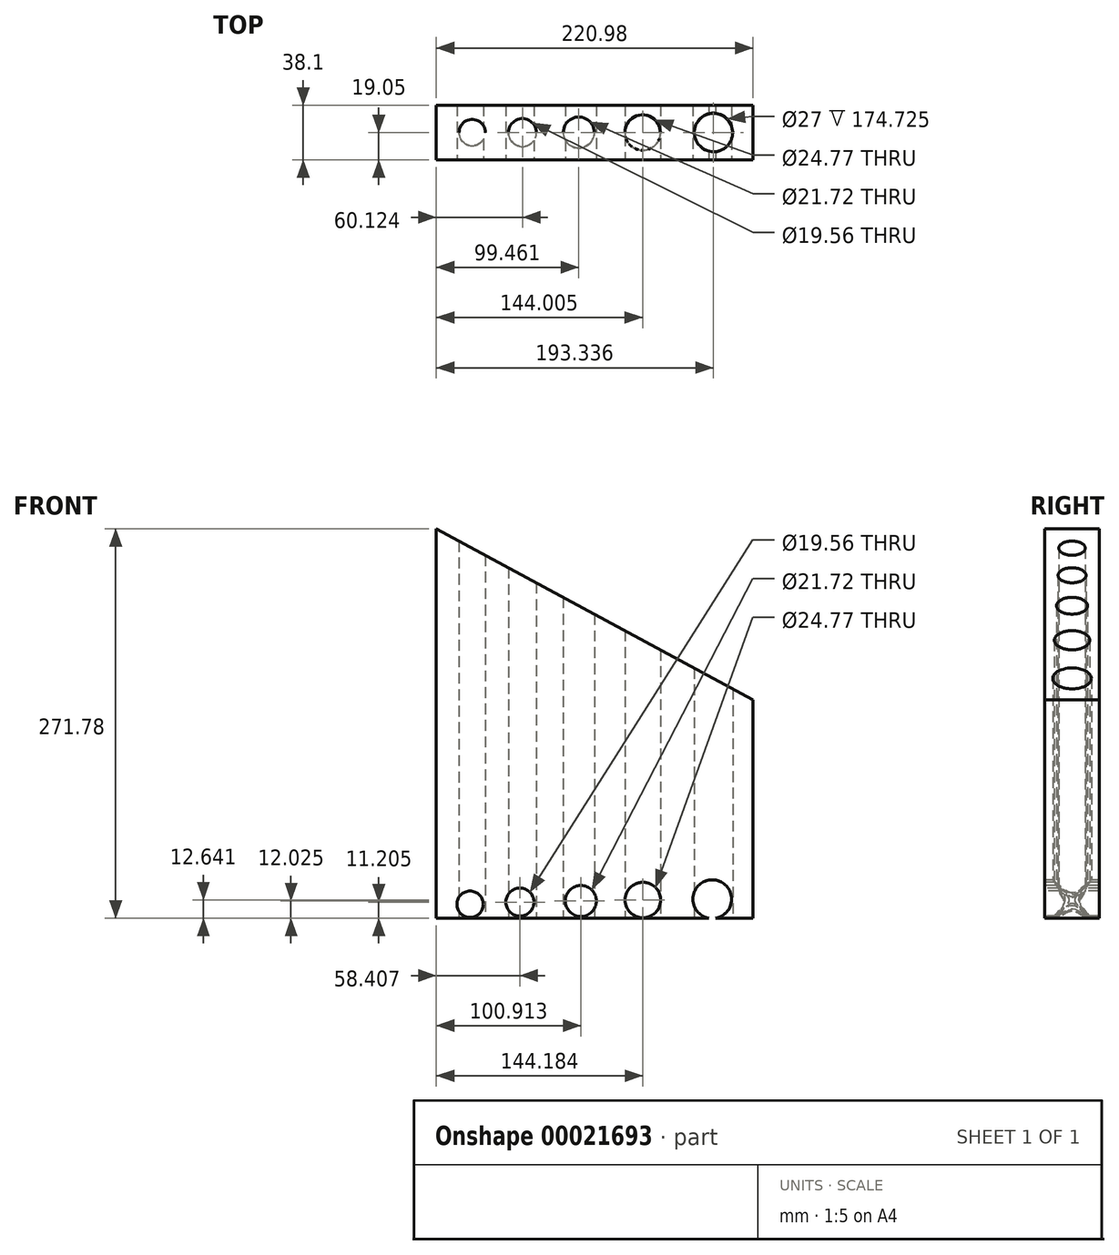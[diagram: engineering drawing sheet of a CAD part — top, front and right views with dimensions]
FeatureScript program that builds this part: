
annotation { "Feature Type Name" : "Feature", "Feature Type Description" : "" }
export const myFeature = defineFeature(function(context is Context, id is Id, definition is map)
    precondition{}
    {
        {
            var Q0;
            Q0=qCreatedBy(makeId("Front.planeOp"),FACE);
            var sketch = newSketch(context, id + "F0", { "sketchPlane" : qUnion([Q0])});
            skLineSegment(sketch, "E0.bottom", {"start": v(-75.01, 96.53) * mm, "end": v(145.97, 96.53) * mm});
            skLineSegment(sketch, "E0.top", {"start": v(-75.01, -55.87) * mm, "end": v(145.97, -55.87) * mm});
            skLineSegment(sketch, "E0.left", {"start": v(-75.01, 96.53) * mm, "end": v(-75.01, -55.87) * mm});
            skLineSegment(sketch, "E0.right", {"start": v(145.97, 96.53) * mm, "end": v(145.97, -55.87) * mm});
            skLineSegment(sketch, "E1", {"start": v(-75.01, 96.53) * mm, "end": v(-75.01, 215.9) * mm});
            skLineSegment(sketch, "E2", {"start": v(-75.01, 215.9) * mm, "end": v(145.97, 96.53) * mm});
            skSolve(sketch);
        }
        {
            var Q0;
            Q0 = qSketchRegion(id + "F0", true);
            extrude(context, id + "F1", {"entities" : qUnion([Q0]), "depth" : 38.1 * mm});
        }
        {
            var Q0;
            Q0=makeQuery(id+"F1.opExtrude","SWEPT_FACE",FACE,{"disambiguationData":[OSD([sQuery(id+"F0.wireOp",EDGE,"E0.top")])]});
            var sketch = newSketch(context, id + "F2", { "sketchPlane" : qUnion([Q0])});
            skLineSegment(sketch, "E3", {"start": v(-75.01, 19.05) * mm, "end": v(145.97, 19.05) * mm});
            skCircle(sketch, "E4", {"center": v(-49.95, 19.05) * mm, "radius": 9.2 * mm});
            skCircle(sketch, "E5", {"center": v(-14.89, 19.05) * mm, "radius": 9.78 * mm});
            skCircle(sketch, "E6", {"center": v(24.45, 19.05) * mm, "radius": 10.86 * mm});
            skCircle(sketch, "E7", {"center": v(118.33, 19.05) * mm, "radius": 14.58 * mm});
            skCircle(sketch, "E8", {"center": v(69, 19.05) * mm, "radius": 12.38 * mm});
            skSolve(sketch);
        }
        {
            var Q0;
            Q0=sQuery(id+"F2.wireOp",VERTEX,"E4.center");
            var Q1;
            Q1=makeQuery(id+"F1.opExtrude","SWEPT_BODY",BODY,{"disambiguationData":[OSD([sQuery(id+"F0.wireOp",EDGE,"E0.top"),sQuery(id+"F0.wireOp",EDGE,"E0.left"),sQuery(id+"F0.wireOp",EDGE,"E0.right"),sQuery(id+"F0.wireOp",EDGE,"E1"),sQuery(id+"F0.wireOp",EDGE,"E2")])]});
            hole(context, id + "F3", {"style" : HoleStyle.SIMPLE, "holeDiameter" : 18.41 * mm, "endStyle" : HoleEndStyle.THROUGH, "locations" : qUnion([Q0]), "scope" : qUnion([Q1])});
        }
        {
            var Q0;
            Q0=sQuery(id+"F2.wireOp",VERTEX,"E5.center");
            var Q1;
            Q1=makeQuery(id+"F1.opExtrude","SWEPT_BODY",BODY,{"disambiguationData":[OSD([sQuery(id+"F0.wireOp",EDGE,"E0.top"),sQuery(id+"F0.wireOp",EDGE,"E0.left"),sQuery(id+"F0.wireOp",EDGE,"E0.right"),sQuery(id+"F0.wireOp",EDGE,"E1"),sQuery(id+"F0.wireOp",EDGE,"E2")])]});
            hole(context, id + "F4", {"style" : HoleStyle.SIMPLE, "holeDiameter" : 19.56 * mm, "endStyle" : HoleEndStyle.THROUGH, "locations" : qUnion([Q0]), "scope" : qUnion([Q1])});
        }
        {
            var Q0;
            Q0=sQuery(id+"F2.wireOp",VERTEX,"E6.center");
            var Q1;
            Q1=makeQuery(id+"F1.opExtrude","SWEPT_BODY",BODY,{"disambiguationData":[OSD([sQuery(id+"F0.wireOp",EDGE,"E0.top"),sQuery(id+"F0.wireOp",EDGE,"E0.left"),sQuery(id+"F0.wireOp",EDGE,"E0.right"),sQuery(id+"F0.wireOp",EDGE,"E1"),sQuery(id+"F0.wireOp",EDGE,"E2")])]});
            hole(context, id + "F5", {"style" : HoleStyle.SIMPLE, "holeDiameter" : 21.72 * mm, "endStyle" : HoleEndStyle.THROUGH, "locations" : qUnion([Q0]), "scope" : qUnion([Q1])});
        }
        {
            var Q0;
            Q0=sQuery(id+"F2.wireOp",VERTEX,"E8.center");
            var Q1;
            Q1=makeQuery(id+"F1.opExtrude","SWEPT_BODY",BODY,{"disambiguationData":[OSD([sQuery(id+"F0.wireOp",EDGE,"E0.top"),sQuery(id+"F0.wireOp",EDGE,"E0.left"),sQuery(id+"F0.wireOp",EDGE,"E0.right"),sQuery(id+"F0.wireOp",EDGE,"E1"),sQuery(id+"F0.wireOp",EDGE,"E2")])]});
            hole(context, id + "F6", {"style" : HoleStyle.SIMPLE, "holeDiameter" : 24.76 * mm, "endStyle" : HoleEndStyle.THROUGH, "locations" : qUnion([Q0]), "scope" : qUnion([Q1])});
        }
        {
            var Q0;
            Q0=makeQuery(id+"F1.opExtrude","CAP_FACE",FACE,{"disambiguationData":[OSD([sQuery(id+"F0.wireOp",EDGE,"E0.top"),sQuery(id+"F0.wireOp",EDGE,"E0.left"),sQuery(id+"F0.wireOp",EDGE,"E0.right"),sQuery(id+"F0.wireOp",EDGE,"E1"),sQuery(id+"F0.wireOp",EDGE,"E2")])],"isStart":false});
            var sketch = newSketch(context, id + "F7", { "sketchPlane" : qUnion([Q0])});
            skCircle(sketch, "E9.cCircle", {"center": v(-51.4, -46.13) * mm, "radius": 9.2 * mm, "construction": true});
            skLineSegment(sketch, "E9.0", {"start": v(-60.6, -55.34) * mm, "end": v(-60.6, -36.93) * mm});
            skLineSegment(sketch, "E9.1", {"start": v(-60.6, -36.93) * mm, "end": v(-42.2, -36.93) * mm});
            skLineSegment(sketch, "E9.2", {"start": v(-42.2, -36.93) * mm, "end": v(-42.2, -55.34) * mm});
            skLineSegment(sketch, "E9.3", {"start": v(-42.2, -55.34) * mm, "end": v(-60.6, -55.34) * mm});
            skPoint(sketch, "E9.0.midPoint", {"position": v(-60.6, -46.13) * mm});
            skLineSegment(sketch, "E10.1", {"start": v(-26.37, -35.69) * mm, "end": v(-6.81, -35.69) * mm});
            skLineSegment(sketch, "E10.2", {"start": v(-6.81, -35.69) * mm, "end": v(-6.81, -55.25) * mm});
            skLineSegment(sketch, "E10.3", {"start": v(-6.81, -55.25) * mm, "end": v(-26.37, -55.25) * mm});
            skLineSegment(sketch, "E10.0", {"start": v(-26.37, -55.25) * mm, "end": v(-26.37, -35.69) * mm});
            skLineSegment(sketch, "E11.1", {"start": v(19.17, 93.32) * mm, "end": v(20.43, 93.32) * mm});
            skLineSegment(sketch, "E12.1", {"start": v(56.78, -30.08) * mm, "end": v(81.55, -30.08) * mm});
            skLineSegment(sketch, "E12.2", {"start": v(81.55, -30.08) * mm, "end": v(81.55, -54.84) * mm});
            skLineSegment(sketch, "E12.3", {"start": v(81.55, -54.84) * mm, "end": v(56.78, -54.84) * mm});
            skLineSegment(sketch, "E12.0", {"start": v(56.78, -54.84) * mm, "end": v(56.78, -30.08) * mm});
            skLineSegment(sketch, "E13.1", {"start": v(14.32, -32.98) * mm, "end": v(36.04, -32.98) * mm});
            skLineSegment(sketch, "E13.2", {"start": v(36.04, -32.98) * mm, "end": v(36.04, -54.7) * mm});
            skLineSegment(sketch, "E13.3", {"start": v(36.04, -54.7) * mm, "end": v(14.32, -54.7) * mm});
            skLineSegment(sketch, "E13.0", {"start": v(14.32, -54.7) * mm, "end": v(14.32, -32.98) * mm});
            skLineSegment(sketch, "E14.bottom", {"start": v(104.2, -28.87) * mm, "end": v(131.2, -28.87) * mm});
            skLineSegment(sketch, "E14.top", {"start": v(104.2, -55.87) * mm, "end": v(131.2, -55.87) * mm});
            skLineSegment(sketch, "E14.left", {"start": v(104.2, -28.87) * mm, "end": v(104.2, -55.87) * mm});
            skLineSegment(sketch, "E14.right", {"start": v(131.2, -28.87) * mm, "end": v(131.2, -55.87) * mm});
            skSolve(sketch);
        }
        {
            var Q0;
            Q0=sQuery(id+"F2.wireOp",VERTEX,"E7.center");
            var Q1;
            Q1=makeQuery(id+"F1.opExtrude","SWEPT_BODY",BODY,{"disambiguationData":[OSD([sQuery(id+"F0.wireOp",EDGE,"E0.top"),sQuery(id+"F0.wireOp",EDGE,"E0.left"),sQuery(id+"F0.wireOp",EDGE,"E0.right"),sQuery(id+"F0.wireOp",EDGE,"E1"),sQuery(id+"F0.wireOp",EDGE,"E2")])]});
            hole(context, id + "F8", {"style" : HoleStyle.SIMPLE, "holeDiameter" : 27 * mm, "endStyle" : HoleEndStyle.THROUGH, "locations" : qUnion([Q0]), "scope" : qUnion([Q1])});
        }
        {
            var Q0;
            Q0=sQuery(id+"F7.wireOp",VERTEX,"E9.cCircle.center");
            var Q1;
            Q1=makeQuery(id+"F1.opExtrude","SWEPT_BODY",BODY,{"disambiguationData":[OSD([sQuery(id+"F0.wireOp",EDGE,"E0.top"),sQuery(id+"F0.wireOp",EDGE,"E0.left"),sQuery(id+"F0.wireOp",EDGE,"E0.right"),sQuery(id+"F0.wireOp",EDGE,"E1"),sQuery(id+"F0.wireOp",EDGE,"E2")])]});
            hole(context, id + "F9", {"style" : HoleStyle.SIMPLE, "holeDiameter" : 18.41 * mm, "endStyle" : HoleEndStyle.THROUGH, "locations" : qUnion([Q0]), "scope" : qUnion([Q1])});
        }
        {
            var Q0;
            Q0=makeQuery(id+"F7.imprint","IMPRINT",FACE,{"disambiguationData":[TD([[makeQuery(id+"F7.imprint","IMPRINT",EDGE,{"derivedFrom":sQuery(id+"F7.wireOp",EDGE,"E9.0")}),1.0]])]});
            var sketch = newSketch(context, id + "F10", { "sketchPlane" : qUnion([Q0])});
            skLineSegment(sketch, "E15", {"start": v(-7.55, -35.94) * mm, "end": v(-25.65, -53.4) * mm});
            skLineSegment(sketch, "E16", {"start": v(-7.55, -54.04) * mm, "end": v(-25.65, -37.23) * mm});
            skPoint(sketch, "E17", {"position": v(-16.6, -44.67) * mm});
            skLineSegment(sketch, "E18", {"start": v(14.42, -55.33) * mm, "end": v(36.4, -33.35) * mm});
            skLineSegment(sketch, "E19", {"start": v(37.04, -55.33) * mm, "end": v(16.36, -34) * mm});
            skLineSegment(sketch, "E20", {"start": v(56.43, -55.98) * mm, "end": v(80.99, -31.42) * mm});
            skLineSegment(sketch, "E21", {"start": v(56.43, -29.48) * mm, "end": v(80.99, -55.98) * mm});
            skLineSegment(sketch, "E22", {"start": v(104.25, -57.27) * mm, "end": v(128.81, -30.12) * mm});
            skLineSegment(sketch, "E23", {"start": v(102.32, -28.83) * mm, "end": v(134.49, -57.94) * mm});
            skPoint(sketch, "E24", {"position": v(25.9, -43.84) * mm});
            skPoint(sketch, "E25", {"position": v(69.17, -43.23) * mm});
            skPoint(sketch, "E26", {"position": v(117.53, -42.6) * mm});
            skSolve(sketch);
        }
        {
            var Q0;
            Q0=sQuery(id+"F10.wireOp",VERTEX,"E17");
            var Q1;
            Q1=makeQuery(id+"F1.opExtrude","SWEPT_BODY",BODY,{"disambiguationData":[OSD([sQuery(id+"F0.wireOp",EDGE,"E0.top"),sQuery(id+"F0.wireOp",EDGE,"E0.left"),sQuery(id+"F0.wireOp",EDGE,"E0.right"),sQuery(id+"F0.wireOp",EDGE,"E1"),sQuery(id+"F0.wireOp",EDGE,"E2")])]});
            hole(context, id + "F11", {"style" : HoleStyle.SIMPLE, "holeDiameter" : 19.56 * mm, "endStyle" : HoleEndStyle.THROUGH, "locations" : qUnion([Q0]), "scope" : qUnion([Q1])});
        }
        {
            var Q0;
            Q0=sQuery(id+"F10.wireOp",VERTEX,"E24");
            var Q1;
            Q1=makeQuery(id+"F1.opExtrude","SWEPT_BODY",BODY,{"disambiguationData":[OSD([sQuery(id+"F0.wireOp",EDGE,"E0.top"),sQuery(id+"F0.wireOp",EDGE,"E0.left"),sQuery(id+"F0.wireOp",EDGE,"E0.right"),sQuery(id+"F0.wireOp",EDGE,"E1"),sQuery(id+"F0.wireOp",EDGE,"E2")])]});
            hole(context, id + "F12", {"style" : HoleStyle.SIMPLE, "holeDiameter" : 21.72 * mm, "endStyle" : HoleEndStyle.THROUGH, "locations" : qUnion([Q0]), "scope" : qUnion([Q1])});
        }
        {
            var Q0;
            Q0=sQuery(id+"F10.wireOp",VERTEX,"E25");
            var Q1;
            Q1=makeQuery(id+"F1.opExtrude","SWEPT_BODY",BODY,{"disambiguationData":[OSD([sQuery(id+"F0.wireOp",EDGE,"E0.top"),sQuery(id+"F0.wireOp",EDGE,"E0.left"),sQuery(id+"F0.wireOp",EDGE,"E0.right"),sQuery(id+"F0.wireOp",EDGE,"E1"),sQuery(id+"F0.wireOp",EDGE,"E2")])]});
            hole(context, id + "F13", {"style" : HoleStyle.SIMPLE, "holeDiameter" : 24.76 * mm, "endStyle" : HoleEndStyle.THROUGH, "locations" : qUnion([Q0]), "scope" : qUnion([Q1])});
        }
        {
            var Q0;
            Q0=sQuery(id+"F10.wireOp",VERTEX,"E26");
            var Q1;
            Q1=makeQuery(id+"F1.opExtrude","SWEPT_BODY",BODY,{"disambiguationData":[OSD([sQuery(id+"F0.wireOp",EDGE,"E0.top"),sQuery(id+"F0.wireOp",EDGE,"E0.left"),sQuery(id+"F0.wireOp",EDGE,"E0.right"),sQuery(id+"F0.wireOp",EDGE,"E1"),sQuery(id+"F0.wireOp",EDGE,"E2")])]});
            hole(context, id + "F14", {"style" : HoleStyle.SIMPLE, "holeDiameter" : 27 * mm, "endStyle" : HoleEndStyle.THROUGH, "locations" : qUnion([Q0]), "scope" : qUnion([Q1])});
        }
    });
